# Revit family: RF3_Recessed Square Luminaire
name_source: partatom
category: Lighting Fixtures
revit_build: Autodesk Revit MEP 2013 (Build: 20130531_2115(x64)
units: mm (PartAtom-declared; Revit-internal decimal feet)

## types (1)
- 3x14W T5 Flourescent Recessed Luminaire
    Apparent Load = 42 VA
    Attachment = Whitecroft Lighting_Acrylic
    Body = Whitecroft Lighting_Steel_White_RAL9003
    Color Filter = 16777215
    Control Gear = High Frequency
    Default Elevation = 1200 mm
    Description = Direct/indirect T5 or TC-L luminaire. Single cell Hexaprism optic incorporating Intermediate Brightness Zone element to diffuse light and graduate brightness across the ceiling, mounted in a steel body painted white with optional air handling conversion as standard  as Whitecroft Lighting SOFTLIGHTER
    Dimming Lamp Color Temperature Shift = <None>
    Drawing Reference = Refer to "Read Me" File
    Emergency = 3HR MAINT
    Emit from Line Length = 610 mm
    Lamp = 3x14W T5
    Length = 600 mm
    Light Body = Light Body
    Light Output Ratio = 81.99%
    Light Type = RF3
    Load Classification = Ltg
    Manufacturer = Whitecroft Lighting
    Optic = Whitecroft Lighting_Acrylic
    Part Number = SFSH220PSTEM
    Photometric Web File = SFSH220PXT.IES
    Single_Cell = Yes
    Tilt Angle = 0.00°
    Twin_Cell = No
    Type Comments = For Emergency Central Monitoring and control replace 'EM' with '/EP'
    URL = www.whitecroftlighting.com
    Weight (Kg) = 5.5
    Width = 600 mm

## geometry (parser evidence)
native form markers: Blend x4, Sweep x1
no freeform markers — native parametric forms only
